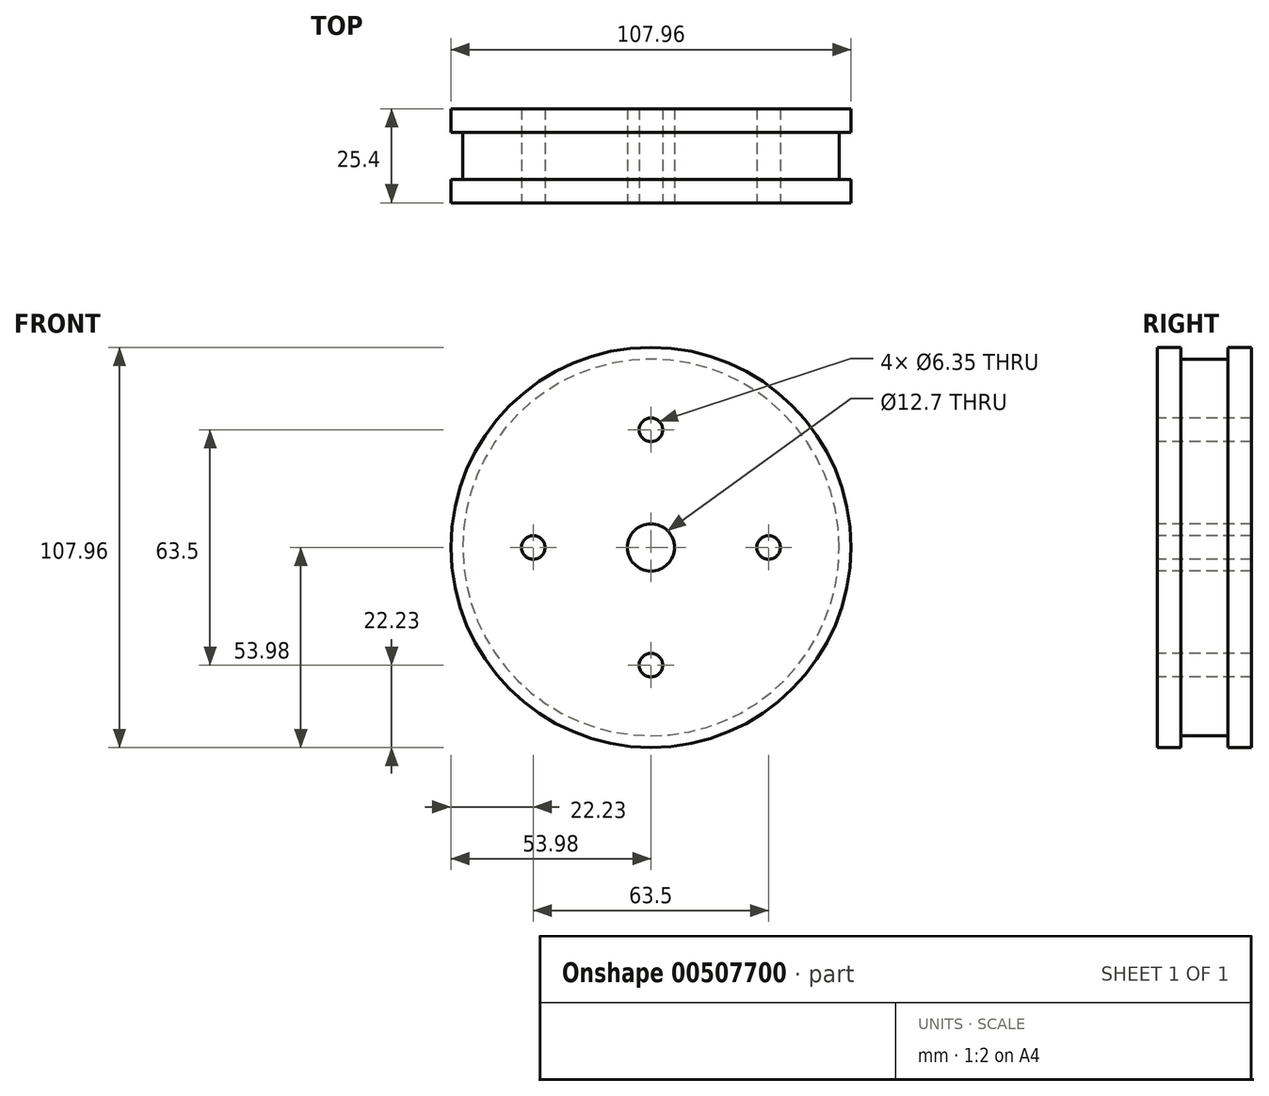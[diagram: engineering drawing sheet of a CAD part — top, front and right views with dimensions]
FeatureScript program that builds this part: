
annotation { "Feature Type Name" : "Feature", "Feature Type Description" : "" }
export const myFeature = defineFeature(function(context is Context, id is Id, definition is map)
    precondition{}
    {
        {
            var Q0;
            Q0=qCreatedBy(makeId("Front.planeOp"),FACE);
            var sketch = newSketch(context, id + "F0", { "sketchPlane" : qUnion([Q0])});
            skCircle(sketch, "E0", {"center": v(0, 0) * mm, "radius": 53.98 * mm});
            skSolve(sketch);
        }
        {
            var Q0;
            Q0 = qSketchRegion(id + "F0", true);
            extrude(context, id + "F1", {"entities" : qUnion([Q0]), "depth" : 6.35 * mm, "offsetDistance" : 25.4 * mm});
        }
        {
            var Q0;
            Q0=makeQuery(id+"F1.opExtrude","CAP_FACE",FACE,{"disambiguationData":[OSD([sQuery(id+"F0.wireOp",EDGE,"E0")])],"isStart":false});
            var sketch = newSketch(context, id + "F2", { "sketchPlane" : qUnion([Q0])});
            skCircle(sketch, "E1", {"center": v(0, 0) * mm, "radius": 50.8 * mm});
            skSolve(sketch);
        }
        {
            var Q0;
            Q0 = qSketchRegion(id + "F2", true);
            extrude(context, id + "F3", {"entities" : qUnion([Q0]), "operationType" : NewBodyOperationType.ADD, "depth" : 12.7 * mm, "offsetDistance" : 25.4 * mm});
        }
        {
            var Q0;
            Q0=makeQuery(id+"F3.opExtrude","CAP_FACE",FACE,{"disambiguationData":[OSD([sQuery(id+"F2.wireOp",EDGE,"E1")])],"isStart":false});
            var sketch = newSketch(context, id + "F4", { "sketchPlane" : qUnion([Q0])});
            skCircle(sketch, "E2", {"center": v(0, 0) * mm, "radius": 53.98 * mm});
            skSolve(sketch);
        }
        {
            var Q0;
            Q0 = qSketchRegion(id + "F4", true);
            extrude(context, id + "F5", {"entities" : qUnion([Q0]), "operationType" : NewBodyOperationType.ADD, "depth" : 6.35 * mm, "offsetDistance" : 25.4 * mm});
        }
        {
            var Q0;
            Q0=makeQuery(id+"F5.opExtrude","CAP_FACE",FACE,{"disambiguationData":[OSD([sQuery(id+"F4.wireOp",EDGE,"E2")])],"isStart":false});
            var sketch = newSketch(context, id + "F6", { "sketchPlane" : qUnion([Q0])});
            skPoint(sketch, "E3", {"position": v(0, 31.75) * mm});
            skPoint(sketch, "E4", {"position": v(31.75, 0) * mm});
            skPoint(sketch, "E5", {"position": v(-31.75, 0) * mm});
            skPoint(sketch, "E6", {"position": v(0, -31.75) * mm});
            skPoint(sketch, "E7", {"position": v(0, 0) * mm});
            skSolve(sketch);
        }
        {
            var Q0;
            Q0=sQuery(id+"F6.wireOp",VERTEX,"E3");
            var Q1;
            Q1=sQuery(id+"F6.wireOp",VERTEX,"E4");
            var Q2;
            Q2=sQuery(id+"F6.wireOp",VERTEX,"E6");
            var Q3;
            Q3=sQuery(id+"F6.wireOp",VERTEX,"E5");
            var Q4;
            Q4=makeQuery(id+"F1.opExtrude","SWEPT_BODY",BODY,{"disambiguationData":[OSD([sQuery(id+"F0.wireOp",EDGE,"E0")])]});
            hole(context, id + "F7", {"style" : HoleStyle.SIMPLE, "endStyle" : HoleEndStyle.THROUGH, "holeDiameter" : 6.35 * mm, "isTappedThrough" : true, "tappedDepth" : 12.7 * mm, "tapClearance" : 3, "locations" : qUnion([Q0, Q1, Q2, Q3]), "scope" : qUnion([Q4])});
        }
        {
            var Q0;
            Q0=makeQuery(id+"F5.opExtrude","CAP_FACE",FACE,{"disambiguationData":[OSD([sQuery(id+"F4.wireOp",EDGE,"E2")])],"isStart":false});
            var sketch = newSketch(context, id + "F8", { "sketchPlane" : qUnion([Q0])});
            skCircle(sketch, "E8", {"center": v(0, 0) * mm, "radius": 6.35 * mm});
            skSolve(sketch);
        }
        {
            var Q0;
            Q0 = qSketchRegion(id + "F8", true);
            extrude(context, id + "F9", {"entities" : qUnion([Q0]), "operationType" : NewBodyOperationType.REMOVE, "endBound" : BoundingType.THROUGH_ALL, "oppositeDirection" : true, "depth" : 25.4 * mm, "offsetDistance" : 25.4 * mm});
        }
    });
